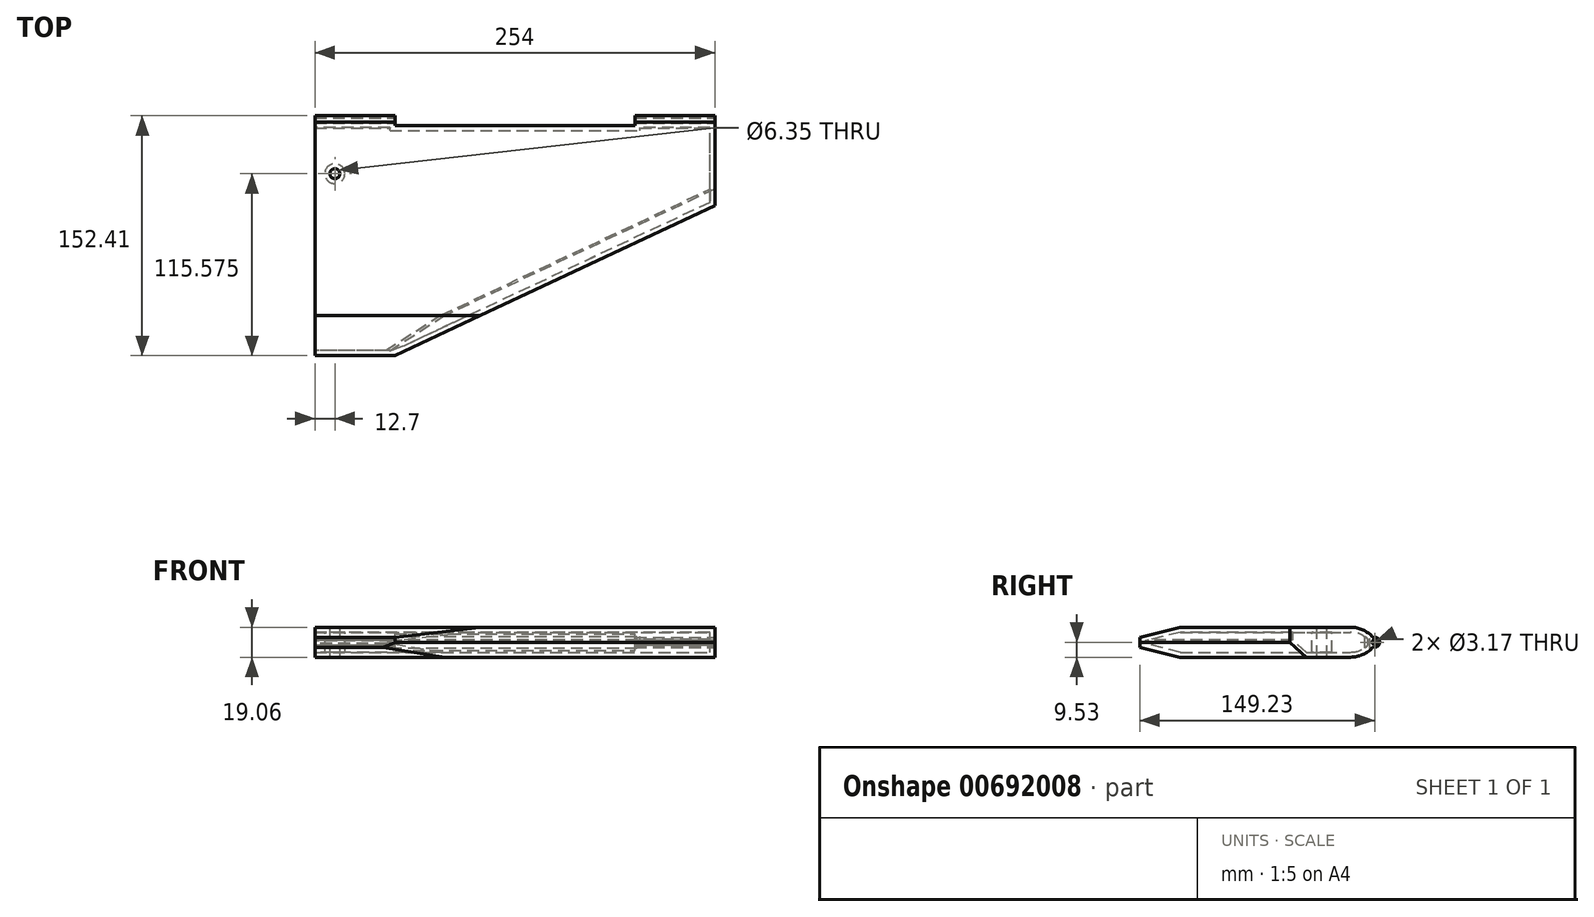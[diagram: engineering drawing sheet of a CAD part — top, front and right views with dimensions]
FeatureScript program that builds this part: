
annotation { "Feature Type Name" : "Feature", "Feature Type Description" : "" }
export const myFeature = defineFeature(function(context is Context, id is Id, definition is map)
    precondition{}
    {
        {
            var Q0;
            Q0=qCreatedBy(makeId("Right.planeOp"),FACE);
            var sketch = newSketch(context, id + "F0", { "sketchPlane" : qUnion([Q0])});
            skLineSegment(sketch, "E0.bottom", {"start": v(-73.03, 9.53) * mm, "end": v(73.03, 9.53) * mm});
            skLineSegment(sketch, "E0.top", {"start": v(-73.03, -9.53) * mm, "end": v(73.03, -9.53) * mm});
            skLineSegment(sketch, "E0.left", {"start": v(-73.03, 9.53) * mm, "end": v(-73.03, -9.53) * mm});
            skLineSegment(sketch, "E0.right", {"start": v(73.03, 9.53) * mm, "end": v(73.03, -9.53) * mm});
            skPoint(sketch, "E0.middle", {"position": v(0, 0) * mm});
            skLineSegment(sketch, "E1", {"start": v(-73.03, -9.53) * mm, "end": v(-73.03, -6.35) * mm});
            skLineSegment(sketch, "E2", {"start": v(-73.03, 9.53) * mm, "end": v(-73.03, 6.35) * mm});
            skLineSegment(sketch, "E3", {"start": v(-73.03, 9.53) * mm, "end": v(-47.62, 9.53) * mm});
            skLineSegment(sketch, "E4", {"start": v(-47.62, 9.53) * mm, "end": v(-47.62, -9.53) * mm});
            skLineSegment(sketch, "E5", {"start": v(-73.03, 0) * mm, "end": v(-73.03, -3.18) * mm});
            skLineSegment(sketch, "E6", {"start": v(-73.03, -3.18) * mm, "end": v(-73.03, 3.17) * mm});
            skLineSegment(sketch, "E7", {"start": v(-47.62, 9.53) * mm, "end": v(-73.03, 3.17) * mm});
            skLineSegment(sketch, "E8", {"start": v(-47.62, -9.53) * mm, "end": v(-73.03, -3.18) * mm});
            skSolve(sketch);
        }
        {
            var Q0;
            Q0 = qSketchRegion(id + "F0", true);
            extrude(context, id + "F1", {"entities" : qUnion([Q0]), "depth" : 254 * mm, "offsetDistance" : 25.4 * mm});
        }
        {
            var Q0;
            Q0=makeQuery(id+"F1.opExtrude","SWEPT_FACE",FACE,{"disambiguationData":[OSD([sQuery(id+"F0.wireOp",EDGE,"E0.bottom")])]});
            var sketch = newSketch(context, id + "F2", { "sketchPlane" : qUnion([Q0])});
            skLineSegment(sketch, "E9", {"start": v(0, -73.03) * mm, "end": v(50.8, -73.03) * mm});
            skLineSegment(sketch, "E10", {"start": v(254, 73.03) * mm, "end": v(254, 22.22) * mm});
            skLineSegment(sketch, "E11", {"start": v(254, 22.23) * mm, "end": v(50.8, -73.03) * mm});
            skSolve(sketch);
        }
        {
            var Q0;
            Q0 = qSketchRegion(id + "F2", true);
            var Q1;
            {var subQ0=sQuery(id+"F2.wireOp",EDGE,"E11");Q1=makeQuery(id+"F2.imprint","IMPRINT",FACE,{"disambiguationData":[TD([[makeQuery(id+"F2.imprint","IMPRINT",EDGE,{"derivedFrom":subQ0}),1.0]])]});}
            extrude(context, id + "F3", {"entities" : qUnion([Q0, Q1]), "operationType" : NewBodyOperationType.REMOVE, "endBound" : BoundingType.THROUGH_ALL, "oppositeDirection" : true, "depth" : 25.4 * mm, "offsetDistance" : 25.4 * mm});
        }
        {
            var Q0;
            Q0=makeQuery(id+"F3.boolean.opBoolean","COPY",EDGE,{"derivedFrom":makeQuery(id+"F3.opExtrude","CAP_EDGE",EDGE,{"disambiguationData":[OSD([sQuery(id+"F2.wireOp",EDGE,"E11")])],"isStart":true})});
            var Q1;
            Q1=makeQuery(id+"F3.boolean.opBoolean","INTERSECT",EDGE,{"derivedFrom":[makeQuery(id+"F1.opExtrude","SWEPT_FACE",FACE,{"disambiguationData":[OSD([sQuery(id+"F0.wireOp",EDGE,"E0.top")])]}),makeQuery(id+"F3.opExtrude","SWEPT_FACE",FACE,{"disambiguationData":[OSD([sQuery(id+"F2.wireOp",EDGE,"E11")])]})]});
            chamfer(context, id + "F4", {"entities" : qUnion([Q0, Q1]), "width" : 9.52 * mm, "tangentPropagation" : true});
        }
        {
            var Q0;
            {var subQ0=sQuery(id+"F0.wireOp",EDGE,"HUjc3N7K-iRee-XVtz-STow-2uoOrDmlqWwK");Q0=makeQuery(id+"F0.imprint","IMPRINT",FACE,{"disambiguationData":[TD([[makeQuery(id+"F0.imprint","IMPRINT",EDGE,{"derivedFrom":subQ0}),1.0]])]});}
            var Q1;
            {var subQ0=sQuery(id+"F0.wireOp",EDGE,"Glp7gCq1-iR8m-ocv8-P6zi-vuiqfP8sHICv");Q1=makeQuery(id+"F0.imprint","IMPRINT",FACE,{"disambiguationData":[TD([[makeQuery(id+"F0.imprint","IMPRINT",EDGE,{"derivedFrom":subQ0}),1.0]])]});}
            var Q2;
            {var subQ0=sQuery(id+"F0.wireOp",EDGE,"E7");Q2=makeQuery(id+"F0.imprint","IMPRINT",FACE,{"disambiguationData":[TD([[makeQuery(id+"F0.imprint","IMPRINT",EDGE,{"derivedFrom":subQ0}),-1.0]])]});}
            var Q3;
            {var subQ0=sQuery(id+"F0.wireOp",EDGE,"E8");Q3=makeQuery(id+"F0.imprint","IMPRINT",FACE,{"disambiguationData":[TD([[makeQuery(id+"F0.imprint","IMPRINT",EDGE,{"derivedFrom":subQ0}),1.0]])]});}
            extrude(context, id + "F5", {"entities" : qUnion([Q0, Q1, Q2, Q3]), "operationType" : NewBodyOperationType.REMOVE, "endBound" : BoundingType.THROUGH_ALL, "depth" : 25.4 * mm, "offsetDistance" : 25.4 * mm});
        }
        {
            var Q0;
            Q0=makeQuery(id+"F1.opExtrude","CAP_FACE",FACE,{"disambiguationData":[OSD([sQuery(id+"F0.wireOp",EDGE,"E0.bottom"),sQuery(id+"F0.wireOp",EDGE,"E0.top"),sQuery(id+"F0.wireOp",EDGE,"E0.left"),sQuery(id+"F0.wireOp",EDGE,"E0.right")])],"isStart":false});
            var sketch = newSketch(context, id + "F6", { "sketchPlane" : qUnion([Q0])});
            skLineSegment(sketch, "E12", {"start": v(73.03, 9.53) * mm, "end": v(73.03, 0) * mm});
            skLineSegment(sketch, "E13", {"start": v(73.03, 0) * mm, "end": v(76.2, 0) * mm});
            skLineSegment(sketch, "E14", {"start": v(76.2, 0) * mm, "end": v(73.02, 9.53) * mm});
            skLineSegment(sketch, "E15", {"start": v(73.03, -9.53) * mm, "end": v(76.2, 0) * mm});
            skCircle(sketch, "E16", {"center": v(76.2, 0) * mm, "radius": 3.18 * mm});
            skCircle(sketch, "E17", {"center": v(76.2, 0) * mm, "radius": 1.59 * mm});
            skSolve(sketch);
        }
        {
            var Q0;
            Q0 = qSketchRegion(id + "F6", true);
            var Q1;
            {var subQ0=sQuery(id+"F6.wireOp",EDGE,"E15");var subQ3=sQuery(id+"F6.wireOp",EDGE,"E16");var subQ4=makeQuery(id+"F6.imprint","INTERSECT",VERTEX,{"derivedFrom":[subQ0,subQ3]});Q1=makeQuery(id+"F6.imprint","IMPRINT",FACE,{"disambiguationData":[TD([[makeQuery(id+"F6.imprint","IMPRINT",EDGE,{"disambiguationData":[TD([[subQ4,1.0]])],"derivedFrom":subQ0}),1.0]])]});}
            extrude(context, id + "F7", {"entities" : qUnion([Q0, Q1]), "operationType" : NewBodyOperationType.ADD, "oppositeDirection" : true, "depth" : 254 * mm, "offsetDistance" : 25.4 * mm});
        }
        {
            var Q0;
            Q0=makeQuery(id+"F1.opExtrude","SWEPT_FACE",FACE,{"disambiguationData":[OSD([sQuery(id+"F0.wireOp",EDGE,"E0.bottom")])]});
            var sketch = newSketch(context, id + "F8", { "sketchPlane" : qUnion([Q0])});
            skLineSegment(sketch, "E18", {"start": v(0, 73.03) * mm, "end": v(50.8, 73.03) * mm});
            skLineSegment(sketch, "E19", {"start": v(50.8, 73.03) * mm, "end": v(203.2, 73.03) * mm});
            skLineSegment(sketch, "E20.top", {"start": v(50.8, 123.83) * mm, "end": v(203.2, 123.83) * mm});
            skLineSegment(sketch, "E20.left", {"start": v(50.8, 73.03) * mm, "end": v(50.8, 123.83) * mm});
            skLineSegment(sketch, "E20.right", {"start": v(203.2, 73.03) * mm, "end": v(203.2, 123.83) * mm});
            skLineSegment(sketch, "E21", {"start": v(0, 73.03) * mm, "end": v(0, 42.55) * mm});
            skLineSegment(sketch, "E22", {"start": v(0, 42.55) * mm, "end": v(12.7, 42.55) * mm});
            skCircle(sketch, "E23", {"center": v(12.7, 42.55) * mm, "radius": 3.18 * mm});
            skSolve(sketch);
        }
        {
            var Q0;
            {var subQ0=sQuery(id+"F6.wireOp",EDGE,"E14");var subQ1=sQuery(id+"F0.wireOp",EDGE,"E0.right");var subQ2=sQuery(id+"F0.wireOp",EDGE,"E0.bottom");var subQ3=sQuery(id+"F6.wireOp",EDGE,"E12");Q0=makeQuery(id+"F0xAijl7oDghpIc_1.boolean.opBoolean","SPLIT",EDGE,{"disambiguationData":[TD([makeQuery(id+"F0xAijl7oDghpIc_1.opExtrude","SWEPT_FACE",FACE,{"disambiguationData":[OSD([sQuery(id+"Fa5dQilrRDUwoAG_1.wireOp",EDGE,"AknoTKYk-zPv5-nR07-hBEs-5b61587hsY2X")])]})])],"derivedFrom":makeQuery(id+"F7.boolean.opBoolean","MERGE",EDGE,{"derivedFrom":[makeQuery(id+"F1.opExtrude","SWEPT_EDGE",EDGE,{"disambiguationData":[OSD([subQ2,subQ1])]}),makeQuery(id+"F7.opExtrude","SWEPT_EDGE",EDGE,{"disambiguationData":[OSD([subQ2,subQ3,subQ0])]})]})});}
            var Q1;
            {var subQ0=sQuery(id+"F6.wireOp",EDGE,"E15");var subQ1=makeQuery(id+"F7.opExtrude","SWEPT_FACE",FACE,{"disambiguationData":[OSD([subQ0])]});var subQ2=sQuery(id+"F0.wireOp",EDGE,"E0.right");var subQ3=sQuery(id+"F0.wireOp",EDGE,"E0.top");var subQ4=makeQuery(id+"F1.opExtrude","SWEPT_FACE",FACE,{"disambiguationData":[OSD([subQ3])]});Q1=makeQuery(id+"F0xAijl7oDghpIc_1.boolean.opBoolean","SPLIT",EDGE,{"disambiguationData":[topologyDisambiguationEdgeConnected([subQ4,subQ1]),TD([makeQuery(id+"F0xAijl7oDghpIc_1.opExtrude","SWEPT_FACE",FACE,{"disambiguationData":[OSD([sQuery(id+"Fa5dQilrRDUwoAG_1.wireOp",EDGE,"AknoTKYk-zPv5-nR07-hBEs-5b61587hsY2X")])]})])],"derivedFrom":makeQuery(id+"F7.boolean.opBoolean","MERGE",EDGE,{"derivedFrom":[makeQuery(id+"F1.opExtrude","SWEPT_EDGE",EDGE,{"disambiguationData":[OSD([subQ3,subQ2])]}),makeQuery(id+"F7.opExtrude","SWEPT_EDGE",EDGE,{"disambiguationData":[OSD([subQ3,subQ2,subQ0])]})]})});}
            fillet(context, id + "F9", {"entities" : qUnion([Q0, Q1]), "tangentPropagation" : true, "radius" : 19.05 * mm, "defaultsChanged" : true, "vertexSettings" : [], "allowEdgeOverflow" : false});
        }
        {
            var Q0;
            Q0 = qSketchRegion(id + "F8", true);
            extrude(context, id + "F10", {"entities" : qUnion([Q0]), "operationType" : NewBodyOperationType.REMOVE, "endBound" : BoundingType.THROUGH_ALL, "oppositeDirection" : true, "depth" : 25.4 * mm, "offsetDistance" : 25.4 * mm});
        }
        {
            var Q0;
            {var subQ0=sQuery(id+"F0.wireOp",EDGE,"E0.right");Q0=makeQuery(id+"F7.boolean.opBoolean","MERGE",FACE,{"derivedFrom":[makeQuery(id+"F1.opExtrude","CAP_FACE",FACE,{"disambiguationData":[OSD([sQuery(id+"F0.wireOp",EDGE,"E0.bottom"),sQuery(id+"F0.wireOp",EDGE,"E0.top"),sQuery(id+"F0.wireOp",EDGE,"E0.left"),subQ0])],"isStart":true}),makeQuery(id+"F7.opExtrude","CAP_FACE",FACE,{"disambiguationData":[OSD([subQ0,sQuery(id+"F6.wireOp",EDGE,"E12"),sQuery(id+"F6.wireOp",EDGE,"E14"),sQuery(id+"F6.wireOp",EDGE,"E15"),sQuery(id+"F6.wireOp",EDGE,"E16"),sQuery(id+"F6.wireOp",EDGE,"E17")])],"isStart":false})]});}
            shell(context, id + "F11", {"entities" : qUnion([Q0]), "thickness" : 3.17 * mm});
        }
    });
